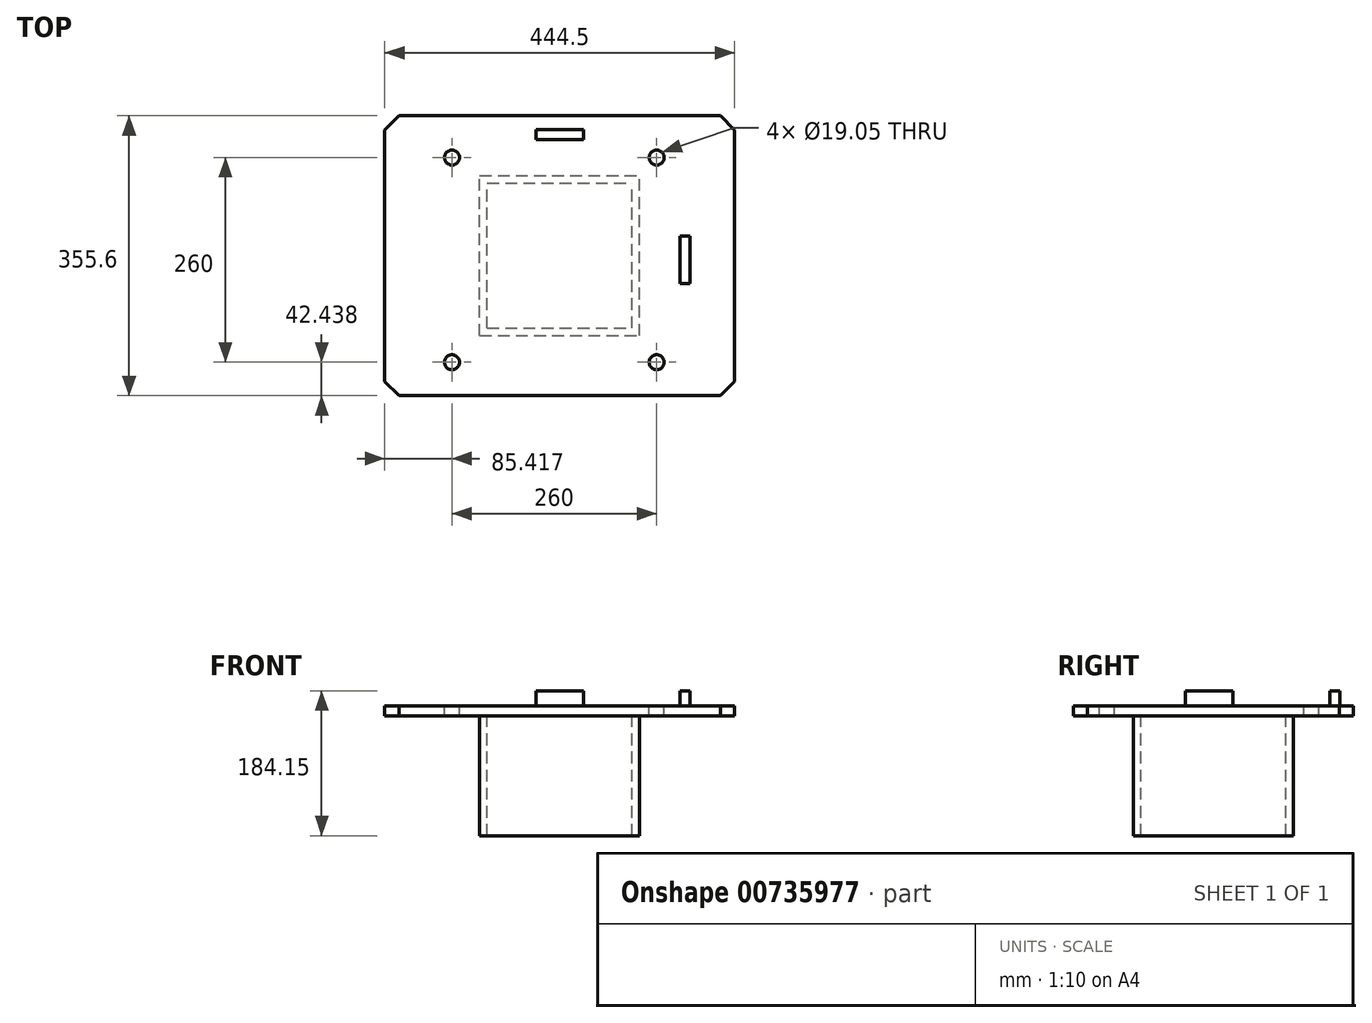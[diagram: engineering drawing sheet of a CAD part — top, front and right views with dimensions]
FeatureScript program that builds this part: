
annotation { "Feature Type Name" : "Feature", "Feature Type Description" : "" }
export const myFeature = defineFeature(function(context is Context, id is Id, definition is map)
    precondition{}
    {
        {
            var Q0;
            Q0=qCreatedBy(makeId("Top.planeOp"),FACE);
            cPlane(context, id + "F0", {"entities" : qUnion([Q0]), "cplaneType" : CPlaneType.OFFSET, "offset" : 304.8 * mm, "width" : 152.4 * mm, "height" : 152.4 * mm});
        }
        {
            var Q0;
            Q0=qCreatedBy(id+"F0.planeOp",FACE);
            var sketch = newSketch(context, id + "F1", { "sketchPlane" : qUnion([Q0])});
            skLineSegment(sketch, "E0.bottom", {"start": v(68.76, 0) * mm, "end": v(477.34, 0) * mm});
            skLineSegment(sketch, "E0.top", {"start": v(68.76, 355.6) * mm, "end": v(477.34, 355.6) * mm});
            skLineSegment(sketch, "E0.left", {"start": v(50.8, 17.96) * mm, "end": v(50.8, 337.64) * mm});
            skLineSegment(sketch, "E0.right", {"start": v(495.3, 17.96) * mm, "end": v(495.3, 337.64) * mm});
            skLineSegment(sketch, "E1", {"start": v(68.76, 355.6) * mm, "end": v(50.8, 337.64) * mm});
            skLineSegment(sketch, "E2", {"start": v(477.34, 355.6) * mm, "end": v(495.3, 337.64) * mm});
            skLineSegment(sketch, "E3", {"start": v(68.76, 0) * mm, "end": v(50.8, 17.96) * mm});
            skLineSegment(sketch, "E4", {"start": v(477.34, 0) * mm, "end": v(495.3, 17.96) * mm});
            skSolve(sketch);
        }
        {
            var Q0;
            {var subQ1=sQuery(id+"F1.wireOp",EDGE,"E0.bottom");Q0=makeQuery(id+"F1.imprint","IMPRINT",FACE,{"disambiguationData":[TD([[makeQuery(id+"F1.imprint","IMPRINT",EDGE,{"derivedFrom":subQ1}),1.0]])]});}
            extrude(context, id + "F2", {"entities" : qUnion([Q0]), "oppositeDirection" : true, "depth" : 12.7 * mm, "offsetDistance" : 25.4 * mm});
        }
        {
            var Q0;
            Q0=makeQuery(id+"F1.imprint","IMPRINT",FACE,{"disambiguationData":[TD([[makeQuery(id+"F1.imprint","IMPRINT",EDGE,{"derivedFrom":sQuery(id+"F1.wireOp",EDGE,"E0.bottom")}),1.0]])]});
            var sketch = newSketch(context, id + "F3", { "sketchPlane" : qUnion([Q0])});
            skCircle(sketch, "E5", {"center": v(396.22, 302.44) * mm, "radius": 9.53 * mm});
            skCircle(sketch, "E6.0.1.0", {"center": v(396.22, 42.44) * mm, "radius": 9.53 * mm});
            skCircle(sketch, "E6.1.0.0", {"center": v(136.22, 302.44) * mm, "radius": 9.53 * mm});
            skCircle(sketch, "E6.1.1.0", {"center": v(136.22, 42.44) * mm, "radius": 9.53 * mm});
            skLineSegment(sketch, "E6.direction1", {"start": v(396.22, 302.44) * mm, "end": v(136.22, 302.44) * mm, "construction": true});
            skLineSegment(sketch, "E6.direction2", {"start": v(396.22, 302.44) * mm, "end": v(396.22, 42.44) * mm, "construction": true});
            skSolve(sketch);
        }
        {
            var Q0;
            Q0=qSketchRegion(id+"F3",true);
            extrude(context, id + "F4", {"entities" : qUnion([Q0]), "operationType" : NewBodyOperationType.REMOVE, "oppositeDirection" : true, "depth" : 12.7 * mm, "offsetDistance" : 25.4 * mm});
        }
        {
            var Q0;
            Q0=makeQuery(id+"F1.imprint","IMPRINT",FACE,{"disambiguationData":[TD([[makeQuery(id+"F1.imprint","IMPRINT",EDGE,{"derivedFrom":sQuery(id+"F1.wireOp",EDGE,"E0.bottom")}),1.0]])]});
            var sketch = newSketch(context, id + "F5", { "sketchPlane" : qUnion([Q0])});
            skLineSegment(sketch, "E7.bottom", {"start": v(243.05, 338.14) * mm, "end": v(303.05, 338.14) * mm});
            skLineSegment(sketch, "E7.top", {"start": v(243.05, 325.44) * mm, "end": v(303.05, 325.44) * mm});
            skLineSegment(sketch, "E7.left", {"start": v(243.05, 338.14) * mm, "end": v(243.05, 325.44) * mm});
            skLineSegment(sketch, "E7.right", {"start": v(303.05, 338.14) * mm, "end": v(303.05, 325.44) * mm});
            skLineSegment(sketch, "E8.bottom", {"start": v(426.05, 202.44) * mm, "end": v(438.75, 202.44) * mm});
            skLineSegment(sketch, "E8.top", {"start": v(426.05, 142.44) * mm, "end": v(438.75, 142.44) * mm});
            skLineSegment(sketch, "E8.left", {"start": v(426.05, 202.44) * mm, "end": v(426.05, 142.44) * mm});
            skLineSegment(sketch, "E8.right", {"start": v(438.75, 202.44) * mm, "end": v(438.75, 142.44) * mm});
            skSolve(sketch);
        }
        {
            var Q0;
            Q0=qSketchRegion(id+"F5",true);
            extrude(context, id + "F6", {"entities" : qUnion([Q0]), "operationType" : NewBodyOperationType.ADD, "depth" : 19.05 * mm, "offsetDistance" : 25.4 * mm});
        }
        {
            var Q0;
            Q0=makeQuery(id+"F2.opExtrude","CAP_FACE",FACE,{"disambiguationData":[OSD([sQuery(id+"F1.wireOp",EDGE,"E0.bottom"),sQuery(id+"F1.wireOp",EDGE,"E0.top"),sQuery(id+"F1.wireOp",EDGE,"E0.left"),sQuery(id+"F1.wireOp",EDGE,"E0.right"),sQuery(id+"F1.wireOp",EDGE,"E1"),sQuery(id+"F1.wireOp",EDGE,"E2"),sQuery(id+"F1.wireOp",EDGE,"E3"),sQuery(id+"F1.wireOp",EDGE,"E4")])],"isStart":false});
            var sketch = newSketch(context, id + "F7", { "sketchPlane" : qUnion([Q0])});
            skLineSegment(sketch, "E9.bottom", {"start": v(171.45, -76.2) * mm, "end": v(374.65, -76.2) * mm});
            skLineSegment(sketch, "E9.top", {"start": v(171.45, -279.4) * mm, "end": v(374.65, -279.4) * mm});
            skLineSegment(sketch, "E9.left", {"start": v(171.45, -76.2) * mm, "end": v(171.45, -279.4) * mm});
            skLineSegment(sketch, "E9.right", {"start": v(374.65, -76.2) * mm, "end": v(374.65, -279.4) * mm});
            skLineSegment(sketch, "E10.0", {"start": v(180.97, -85.72) * mm, "end": v(365.12, -85.72) * mm});
            skLineSegment(sketch, "E10.1", {"start": v(180.97, -85.72) * mm, "end": v(180.97, -269.88) * mm});
            skLineSegment(sketch, "E10.2", {"start": v(180.97, -269.88) * mm, "end": v(365.12, -269.88) * mm});
            skLineSegment(sketch, "E10.3", {"start": v(365.12, -85.72) * mm, "end": v(365.12, -269.88) * mm});
            skSolve(sketch);
        }
        {
            var Q0;
            Q0 = qSketchRegion(id + "F7", true);
            extrude(context, id + "F8", {"entities" : qUnion([Q0]), "operationType" : NewBodyOperationType.ADD, "depth" : 152.4 * mm, "offsetDistance" : 25.4 * mm});
        }
    });
